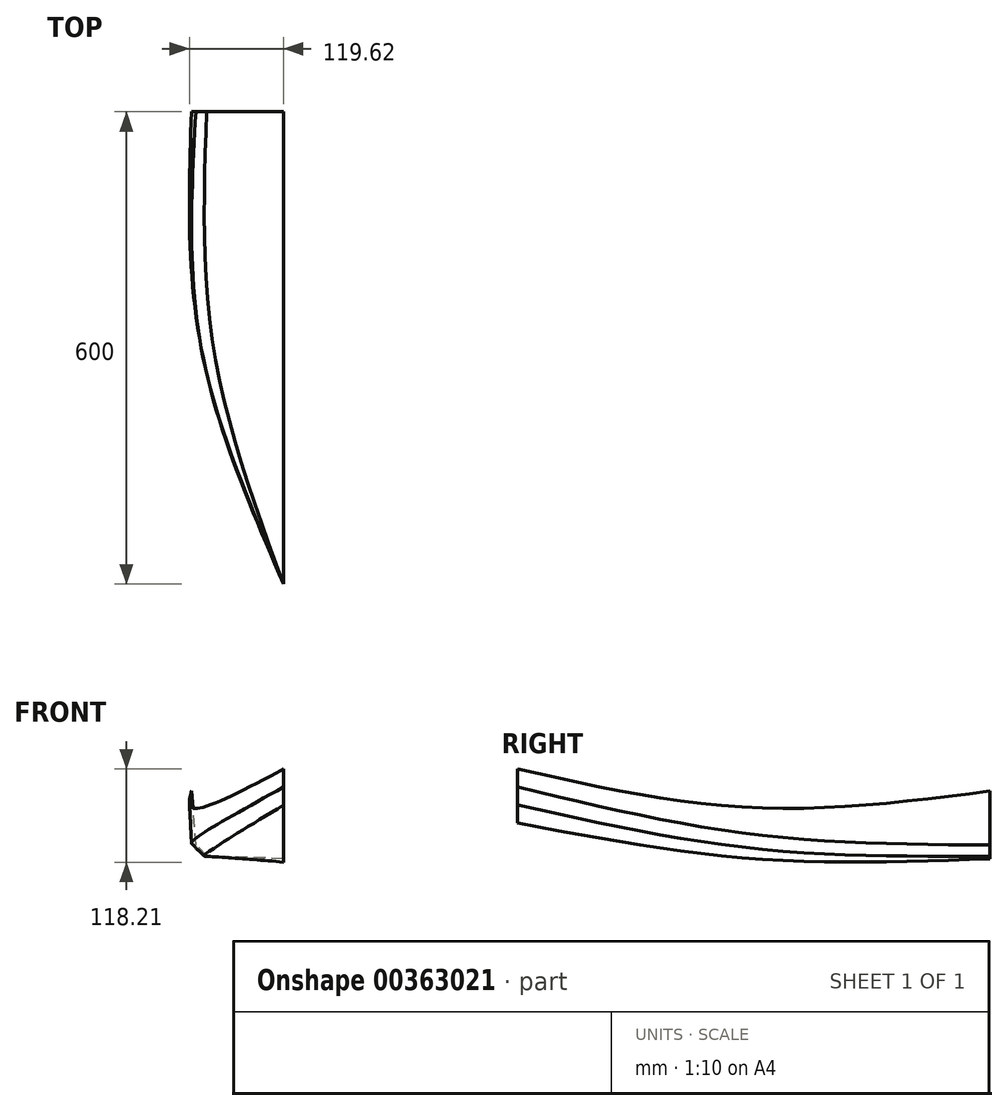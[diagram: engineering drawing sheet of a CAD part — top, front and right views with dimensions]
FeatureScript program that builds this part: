
annotation { "Feature Type Name" : "Feature", "Feature Type Description" : "" }
export const myFeature = defineFeature(function(context is Context, id is Id, definition is map)
    precondition{}
    {
        {
            var Q0;
            Q0=qCreatedBy(makeId("Front.planeOp"),FACE);
            var sketch = newSketch(context, id + "F0", { "sketchPlane" : qUnion([Q0])});
            skLineSegment(sketch, "E0", {"start": v(0, 0) * mm, "end": v(-97.71, 3.42) * mm});
            skLineSegment(sketch, "E1", {"start": v(-97.71, 3.42) * mm, "end": v(-111.38, 17.45) * mm});
            skLineSegment(sketch, "E2", {"start": v(-111.38, 17.45) * mm, "end": v(-117.03, 85.97) * mm});
            skSolve(sketch);
        }
        {
            var Q0;
            Q0=qCreatedBy(makeId("Front.planeOp"),FACE);
            cPlane(context, id + "F1", {"entities" : qUnion([Q0]), "cplaneType" : CPlaneType.OFFSET, "offset" : 300 * mm, "width" : 150 * mm, "height" : 150 * mm});
        }
        {
            var Q0;
            Q0=qCreatedBy(id+"F1.planeOp",FACE);
            var sketch = newSketch(context, id + "F2", { "sketchPlane" : qUnion([Q0])});
            skLineSegment(sketch, "E3", {"start": v(0, 0) * mm, "end": v(-88.9, 13.16) * mm});
            skLineSegment(sketch, "E4", {"start": v(-88.9, 13.16) * mm, "end": v(-104.57, 30.98) * mm});
            skLineSegment(sketch, "E5", {"start": v(-104.57, 30.98) * mm, "end": v(-104.57, 64.77) * mm});
            skSolve(sketch);
        }
        {
            var Q0;
            Q0=qCreatedBy(id+"F1.planeOp",FACE);
            cPlane(context, id + "F3", {"entities" : qUnion([Q0]), "cplaneType" : CPlaneType.OFFSET, "offset" : 300 * mm, "width" : 150 * mm, "height" : 150 * mm});
        }
        {
            var Q0;
            Q0=qCreatedBy(id+"F3.planeOp",FACE);
            var sketch = newSketch(context, id + "F4", { "sketchPlane" : qUnion([Q0])});
            skLineSegment(sketch, "E6", {"start": v(0, 45.5) * mm, "end": v(0, 113.92) * mm});
            skSolve(sketch);
        }
        {
            var Q0;
            Q0 = qSketchRegion(id + "F0", true);
            var Q1;
            Q1 = qSketchRegion(id + "F2", true);
            var Q2;
            Q2 = qSketchRegion(id + "F4", true);
            var Q3;
            Q3 = qConstructionFilter(qBodyType(qCreatedBy(id + "F0" ,EDGE), BodyType.WIRE), ConstructionObject.NO);
            var Q4;
            Q4 = qConstructionFilter(qBodyType(qCreatedBy(id + "F2" ,EDGE), BodyType.WIRE), ConstructionObject.NO);
            var Q5;
            Q5 = qConstructionFilter(qBodyType(qCreatedBy(id + "F4" ,EDGE), BodyType.WIRE), ConstructionObject.NO);
            loft(context, id + "F5", {"bodyType" : ToolBodyType.SURFACE, "sheetProfilesArray" : [{ "sheetProfileEntities" : qUnion([Q0]) }, { "sheetProfileEntities" : qUnion([Q1]) }, { "sheetProfileEntities" : qUnion([Q2]) }], "wireProfilesArray" : [{ "wireProfileEntities" : qUnion([Q3]) }, { "wireProfileEntities" : qUnion([Q4]) }, { "wireProfileEntities" : qUnion([Q5]) }]});
        }
        {
            var Q0;
            Q0=qCreatedBy(makeId("Front.planeOp"),FACE);
            cPlane(context, id + "F6", {"entities" : qUnion([Q0]), "cplaneType" : CPlaneType.OFFSET, "offset" : 100 * mm, "oppositeDirection" : true, "width" : 150 * mm, "height" : 150 * mm});
        }
    });
